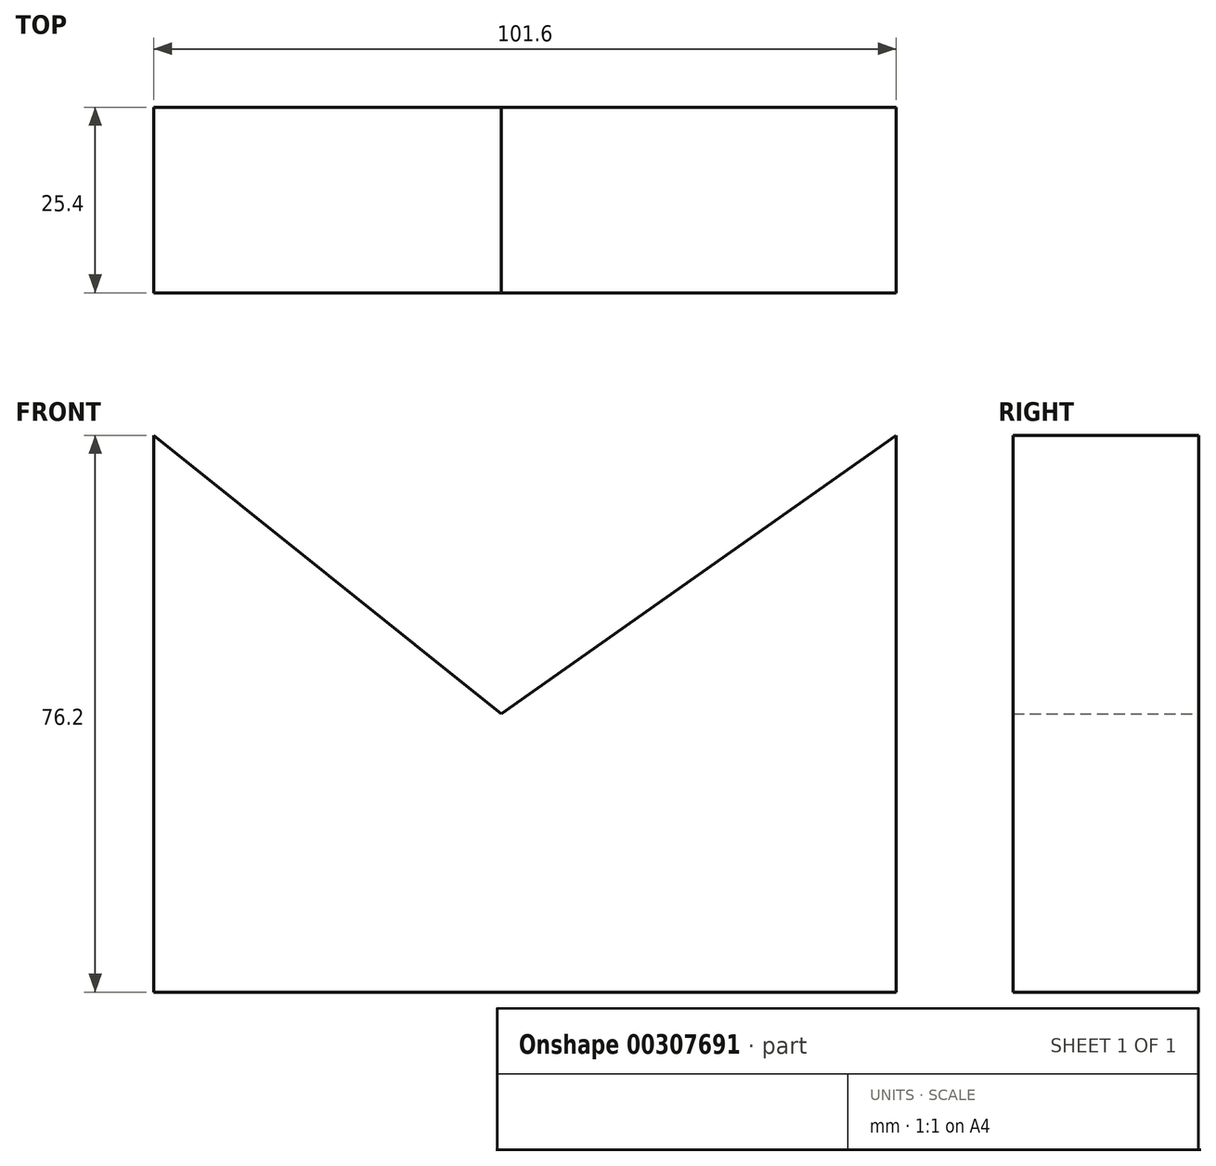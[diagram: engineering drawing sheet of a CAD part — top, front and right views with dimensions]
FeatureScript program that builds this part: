
annotation { "Feature Type Name" : "Feature", "Feature Type Description" : "" }
export const myFeature = defineFeature(function(context is Context, id is Id, definition is map)
    precondition{}
    {
        {
            var Q0;
            Q0=qCreatedBy(makeId("Front.planeOp"),FACE);
            var sketch = newSketch(context, id + "F0", { "sketchPlane" : qUnion([Q0])});
            skLineSegment(sketch, "E0", {"start": v(-43.85, -62.45) * mm, "end": v(57.75, -62.45) * mm});
            skLineSegment(sketch, "E1", {"start": v(57.75, -62.45) * mm, "end": v(57.75, 13.75) * mm});
            skLineSegment(sketch, "E2", {"start": v(-43.85, 13.75) * mm, "end": v(-43.85, -62.45) * mm});
            skLineSegment(sketch, "E3", {"start": v(57.75, 13.75) * mm, "end": v(3.73, -24.35) * mm});
            skPoint(sketch, "E3.endSnap0", {"position": v(57.75, -24.35) * mm});
            skLineSegment(sketch, "E4", {"start": v(3.73, -24.35) * mm, "end": v(-43.85, 13.75) * mm});
            skSolve(sketch);
        }
        {
            var Q0;
            Q0=makeQuery(id+"F0.imprint","IMPRINT",FACE,{"disambiguationData":[TD([[makeQuery(id+"F0.imprint","IMPRINT",EDGE,{"derivedFrom":sQuery(id+"F0.wireOp",EDGE,"E0")}),1.0]])]});
            extrude(context, id + "F1", {"entities" : qUnion([Q0]), "depth" : 25.4 * mm});
        }
    });
